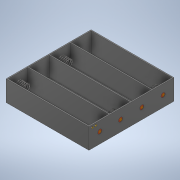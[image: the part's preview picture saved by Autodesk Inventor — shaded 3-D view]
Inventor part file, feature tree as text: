
AUTODESK INVENTOR PART (.ipt)
format: ipt  version: 2020 (Build 240168000, 168)  size: 501,760 bytes
history: native  units: mm
features: sketch x19, other x6, extrude x5, plane x4
ambient origin geometry x8: Origin, YZ Plane, XZ Plane, XY Plane, X Axis, Y Axis, Z Axis, Center Point
bodies: Body1 (feature_tree)
feature tree (34):
  other  "Sólido1"
  extrude  "Extrusión1"  Depth=19.75mm
  extrude  "Extrusión2"  Depth=38.5mm
  plane  "Plano de trabajo2"
  other  "Bobina1"
  plane  "Plano de trabajo3"
  plane  "Plano de trabajo4"
  plane  "Plano de trabajo5"
  other  "Bobina2"
  other  "Bobina3"
  other  "Bobina4"
  extrude  "Extrusión3"  Depth=1.0mm
  extrude  "Extrusión4"  Depth=1.0mm
  sketch  "Boceto10"  dims[d30=10.0mm d31=8.0mm d32=50.0mm d33=0.0mm d34=90.0deg d35=90.0deg d36=0.0mm d37=0.0mm]
  sketch  "Boceto11"  dims[d38=9.0mm]
  sketch  "Boceto12"  dims[d39=9.0mm]
  sketch  "Boceto13"  dims[d40=9.0mm]
  sketch  "Boceto14"  dims[d41=0.0mm d42=0.0mm d43=90.0deg d44=90.0deg d45=0.0mm d46=50.0mm d47=8.0mm d48=10.0mm]
  sketch  "Boceto15"  dims[d49=4.0mm d50=0.5mm]
  extrude  "Extrusión5"  Depth=1.0mm TaperAngle=0.0deg
  sketch  "Boceto17"  dims[d59=4.0mm d60=0.5mm]
  sketch  "Boceto18"  dims[d61=0.0mm d62=0.0mm d63=90.0deg d64=90.0deg d65=0.0mm d66=50.0mm d67=8.0mm d68=10.0mm]
  sketch  "Boceto19"  dims[d69=4.0mm d70=0.5mm]
  sketch  "Boceto20"  dims[d71=1.5mm d72=1.5mm d73=3.0mm d74=2.0mm d75=0.25mm d76=0.0mm d77=4.0mm d78=4.0mm d79=4.0mm d80=4.0mm d81=9.0mm d82=9.125mm d83=9.125mm d84=9.125mm d85=9.125mm d86=0.25mm d87=0.0mm d88=3.0mm d89=4.0mm d90=0.25mm d91=0.0mm]
  sketch  "Boceto1"  dims[d2=19.75mm d3=19.75mm]
  sketch  "Boceto2"  dims[d4=19.75mm d6=38.5mm]
  sketch  "Boceto4"  dims[d10=0.5mm d17=1.0mm d18=1.0mm]
  sketch  "Boceto8"  dims[d28=0.5mm]
  sketch  "Boceto9"  dims[d29=4.0mm]
  sketch  "Boceto16"  dims[d51=0.0mm d52=0.0mm d53=90.0deg d54=90.0deg d55=0.0mm d56=50.0mm d57=8.0mm d58=10.0mm]
  sketch  "Boceto5"  dims[d19=1.0mm d20=1.0mm]
  sketch  "Boceto6"  dims[d21=18.0mm d22=0.0mm d23=1.0mm d24=0.0mm]
  sketch  "Boceto7"  dims[d27=9.0mm]
  other  "Proyectar aristas de corte1"
